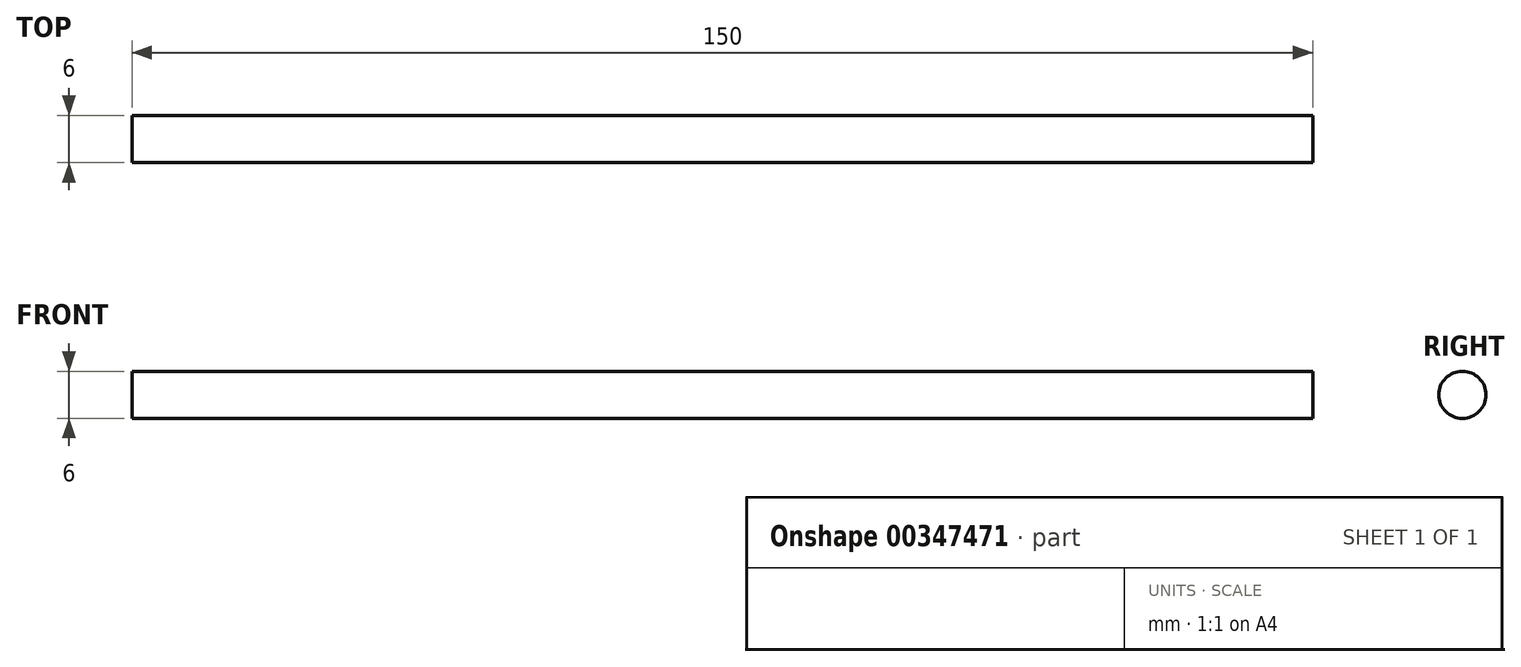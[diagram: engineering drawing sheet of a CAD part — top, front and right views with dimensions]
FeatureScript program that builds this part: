
annotation { "Feature Type Name" : "Feature", "Feature Type Description" : "" }
export const myFeature = defineFeature(function(context is Context, id is Id, definition is map)
    precondition{}
    {
        {
            var Q0;
            Q0=qCreatedBy(makeId("Right.planeOp"),FACE);
            cPlane(context, id + "F0", {"entities" : qUnion([Q0]), "cplaneType" : CPlaneType.OFFSET, "offset" : 260 * mm, "width" : 150 * mm, "height" : 150 * mm});
        }
        {
            var Q0;
            Q0=qCreatedBy(makeId("Front.planeOp"),FACE);
            var sketch = newSketch(context, id + "F1", { "sketchPlane" : qUnion([Q0])});
            skLineSegment(sketch, "E0", {"start": v(0, 0) * mm, "end": v(259.57, 0) * mm});
            skPoint(sketch, "E1", {"position": v(259.57, 5.01) * mm});
            skPoint(sketch, "E2", {"position": v(109.57, 0) * mm});
            skLineSegment(sketch, "E3", {"start": v(109.57, 0) * mm, "end": v(109.57, 3) * mm});
            skLineSegment(sketch, "E4", {"start": v(109.57, 3) * mm, "end": v(259.57, 3) * mm});
            skLineSegment(sketch, "E5", {"start": v(259.57, 3) * mm, "end": v(259.57, 0) * mm});
            skSolve(sketch);
        }
        {
            var Q0;
            Q0=qCreatedBy(makeId("Front.planeOp"),FACE);
            var sketch = newSketch(context, id + "F2", { "sketchPlane" : qUnion([Q0])});
            skLineSegment(sketch, "E6", {"start": v(-12.85, 0) * mm, "end": v(-36.97, 0) * mm});
            skSolve(sketch);
        }
        {
            var Q0;
            Q0 = qSketchRegion(id + "F1", true);
            var Q1;
            Q1=sQuery(id+"F2.wireOp",EDGE,"E6");
            revolve(context, id + "F3", {"entities" : qUnion([Q0]), "axis" : qUnion([Q1]), "revolveType" : RevolveType.FULL});
        }
        {
            var Q0;
            Q0=qCreatedBy(makeId("Front.planeOp"),FACE);
            var sketch = newSketch(context, id + "F4", { "sketchPlane" : qUnion([Q0])});
            skPoint(sketch, "E7", {"position": v(110, 10) * mm});
            skLineSegment(sketch, "E8", {"start": v(110, 10) * mm, "end": v(106, 10) * mm});
            skArc(sketch, "E9", {"start": v(106, 10) * mm, "mid": v(105.27, 14.07) * mm, "end": v(104, 18) * mm});
            skPoint(sketch, "E10", {"position": v(54.57, 16.8) * mm});
            skArc(sketch, "E11", {"start": v(54.57, 16.8) * mm, "mid": v(79.37, 13.65) * mm, "end": v(104, 18) * mm});
            skPoint(sketch, "E12", {"position": v(4.42, 16.8) * mm});
            skArc(sketch, "E13", {"start": v(54.57, 16.8) * mm, "mid": v(29.5, 20.45) * mm, "end": v(4.42, 16.8) * mm});
            skArc(sketch, "E14", {"start": v(4.42, 16.8) * mm, "mid": v(0.97, 8.72) * mm, "end": v(0, 0) * mm});
            skLineSegment(sketch, "E15", {"start": v(110, 10) * mm, "end": v(110, 0) * mm});
            skSolve(sketch);
        }
        {
            var Q0;
            Q0=qCreatedBy(makeId("Front.planeOp"),FACE);
            var sketch = newSketch(context, id + "F5", { "sketchPlane" : qUnion([Q0])});
            skLineSegment(sketch, "E16", {"start": v(-6.6, 0) * mm, "end": v(-13.9, 0) * mm});
            skSolve(sketch);
        }
        {
            var Q0;
            Q0 = qConstructionFilter(qBodyType(qCreatedBy(id + "F4" ,EDGE), BodyType.WIRE), ConstructionObject.NO);
            var Q1;
            Q1=sQuery(id+"F5.wireOp",EDGE,"E16");
            revolve(context, id + "F6", {"bodyType" : ToolBodyType.SURFACE, "surfaceEntities" : qUnion([Q0]), "axis" : qUnion([Q1]), "revolveType" : RevolveType.FULL});
        }
    });
